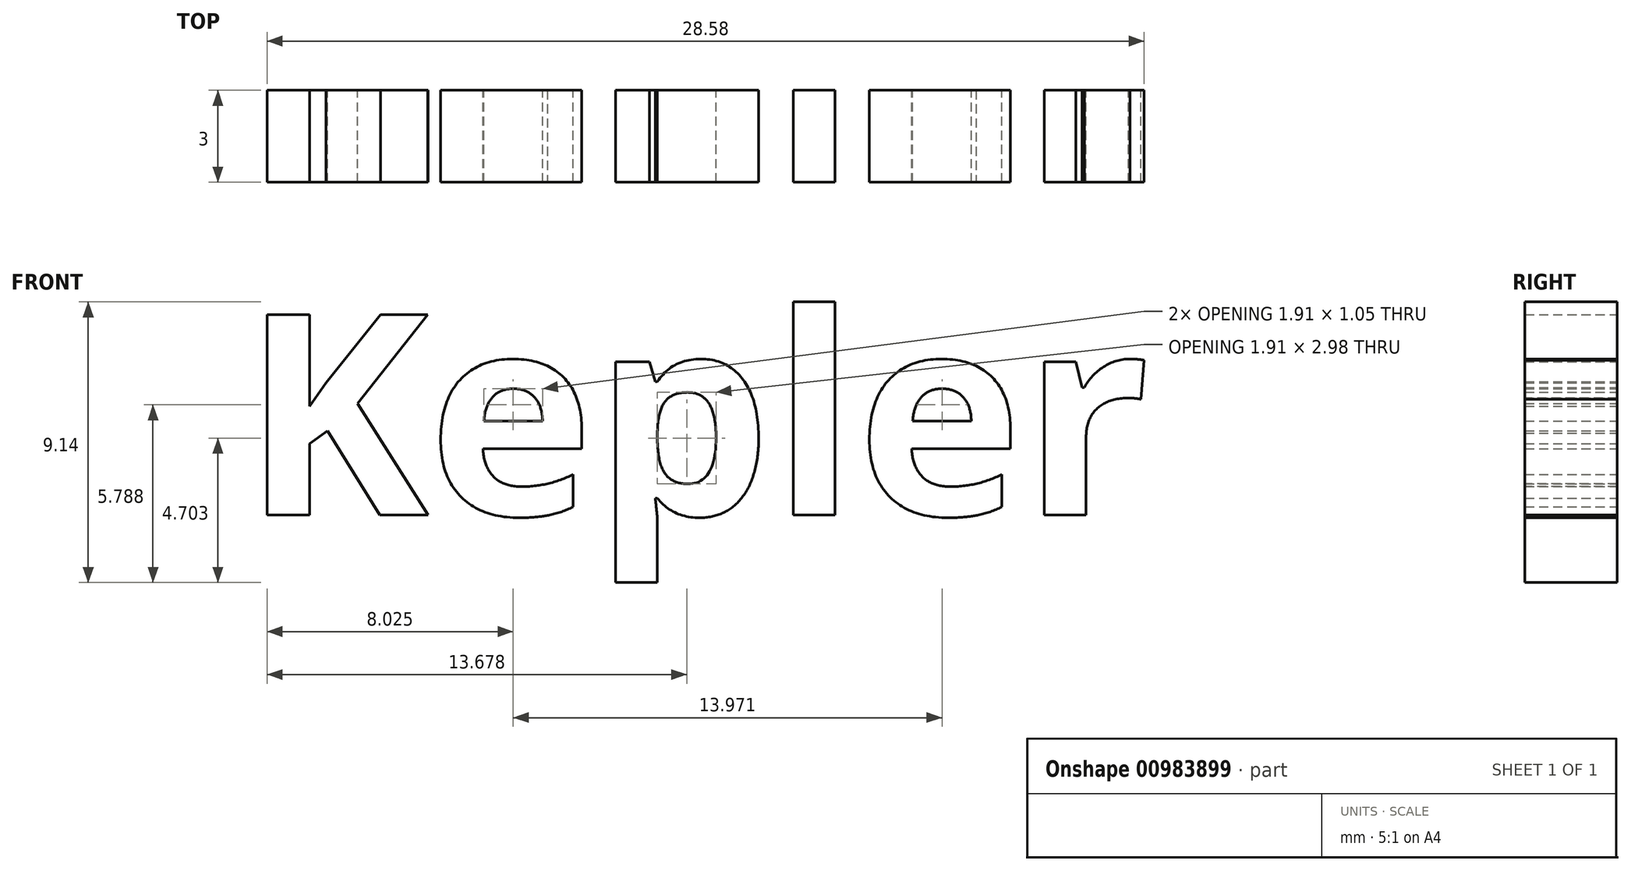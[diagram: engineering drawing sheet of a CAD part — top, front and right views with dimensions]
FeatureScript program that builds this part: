
annotation { "Feature Type Name" : "Feature", "Feature Type Description" : "" }
export const myFeature = defineFeature(function(context is Context, id is Id, definition is map)
    precondition{}
    {
        {
            var Q0;
            Q0=qCreatedBy(makeId("Front.planeOp"),FACE);
            var sketch = newSketch(context, id + "F0", { "sketchPlane" : qUnion([Q0])});
            skText(sketch, "E0", { "text": "Kepler", "fontName": "OpenSans-Bold.ttf"});
            const initialGuessF0  = {"E0": [-0.0056, -0.00269, 1, 0, 0.00658]};
            skSetInitialGuess(sketch, initialGuessF0);
            skSolve(sketch);
        }
        {
            var Q0;
            Q0 = qSketchRegion(id + "F0", true);
            extrude(context, id + "F1", {"entities" : qUnion([Q0]), "depth" : 3 * mm, "offsetDistance" : 25 * mm});
        }
    });
